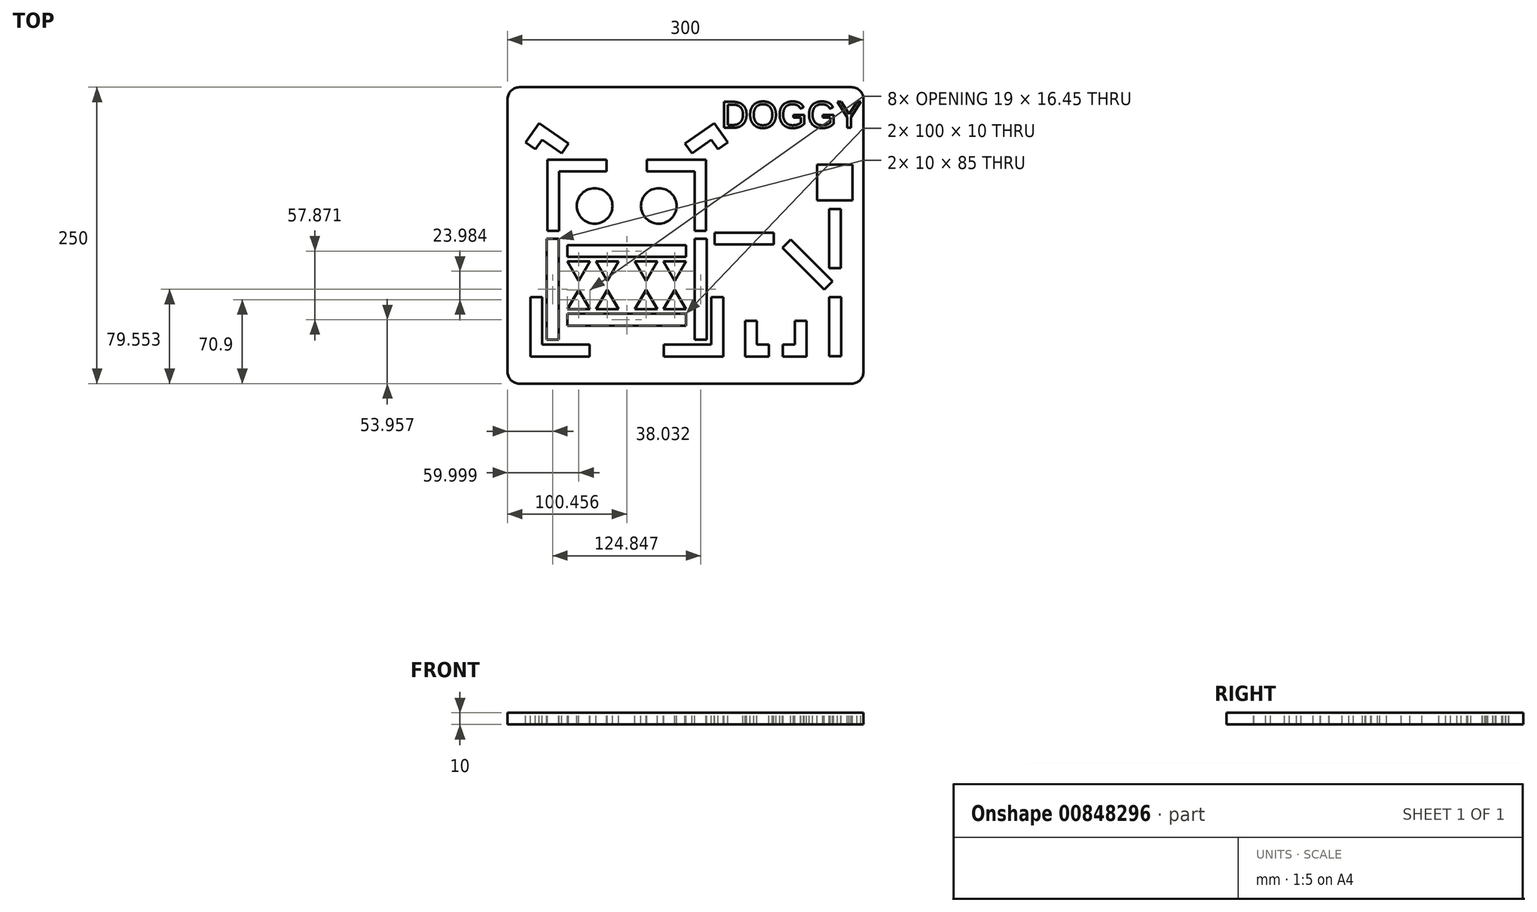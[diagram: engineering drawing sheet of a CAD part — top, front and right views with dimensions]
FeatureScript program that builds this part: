
annotation { "Feature Type Name" : "Feature", "Feature Type Description" : "" }
export const myFeature = defineFeature(function(context is Context, id is Id, definition is map)
    precondition{}
    {
        {
            var Q0;
            Q0=qCreatedBy(makeId("Top.planeOp"),FACE);
            var sketch = newSketch(context, id + "F0", { "sketchPlane" : qUnion([Q0])});
            skLineSegment(sketch, "E0.bottom", {"start": v(-140, 125) * mm, "end": v(140, 125) * mm});
            skLineSegment(sketch, "E0.top", {"start": v(-140, -125) * mm, "end": v(140, -125) * mm});
            skLineSegment(sketch, "E0.left", {"start": v(-150, 115) * mm, "end": v(-150, -115) * mm});
            skLineSegment(sketch, "E0.right", {"start": v(150, 115) * mm, "end": v(150, -115) * mm});
            skPoint(sketch, "E0.middle", {"position": v(0, 0) * mm});
            skPoint(sketch, "E1.visualSharp", {"position": v(-150, 125) * mm});
            skArc(sketch, "E1.filletArc", {"start": v(-140, 125) * mm, "mid": v(-147.07, 122.07) * mm, "end": v(-150, 115) * mm});
            skPoint(sketch, "E2.visualSharp", {"position": v(150, 125) * mm});
            skArc(sketch, "E2.filletArc", {"start": v(150, 115) * mm, "mid": v(147.07, 122.07) * mm, "end": v(140, 125) * mm});
            skPoint(sketch, "E3.visualSharp", {"position": v(150, -125) * mm});
            skArc(sketch, "E3.filletArc", {"start": v(140, -125) * mm, "mid": v(147.07, -122.07) * mm, "end": v(150, -115) * mm});
            skPoint(sketch, "E4.visualSharp", {"position": v(-150, -125) * mm});
            skArc(sketch, "E4.filletArc", {"start": v(-150, -115) * mm, "mid": v(-147.07, -122.07) * mm, "end": v(-140, -125) * mm});
            skSolve(sketch);
        }
        {
            var Q0;
            Q0=makeQuery(id+"F0.imprint","IMPRINT",FACE,{"disambiguationData":[TD([[makeQuery(id+"F0.imprint","IMPRINT",EDGE,{"derivedFrom":sQuery(id+"F0.wireOp",EDGE,"E0.bottom")}),-1.0]])]});
            extrude(context, id + "F1", {"entities" : qUnion([Q0]), "depth" : 10 * mm, "offsetDistance" : 25 * mm});
        }
        {
            var Q0;
            Q0=makeQuery(id+"F1.opExtrude","CAP_FACE",FACE,{"disambiguationData":[OSD([sQuery(id+"F0.wireOp",EDGE,"E0.bottom"),sQuery(id+"F0.wireOp",EDGE,"E0.top"),sQuery(id+"F0.wireOp",EDGE,"E0.left"),sQuery(id+"F0.wireOp",EDGE,"E0.right"),sQuery(id+"F0.wireOp",EDGE,"E1.filletArc"),sQuery(id+"F0.wireOp",EDGE,"E2.filletArc"),sQuery(id+"F0.wireOp",EDGE,"E3.filletArc"),sQuery(id+"F0.wireOp",EDGE,"E4.filletArc")])],"isStart":false});
            var sketch = newSketch(context, id + "F2", { "sketchPlane" : qUnion([Q0])});
            skLineSegment(sketch, "E5.bottom", {"start": v(74.47, -7.65) * mm, "end": v(24.47, -7.65) * mm});
            skLineSegment(sketch, "E5.top", {"start": v(74.47, 2.35) * mm, "end": v(24.47, 2.35) * mm});
            skLineSegment(sketch, "E5.left", {"start": v(74.47, -7.65) * mm, "end": v(74.47, 2.35) * mm});
            skLineSegment(sketch, "E5.right", {"start": v(24.47, -7.65) * mm, "end": v(24.47, 2.35) * mm});
            skPoint(sketch, "E5.middle", {"position": v(49.47, -2.65) * mm});
            skLineSegment(sketch, "E6.bottom", {"start": v(131.14, -51.97) * mm, "end": v(131.14, -101.97) * mm});
            skLineSegment(sketch, "E6.top", {"start": v(121.14, -51.97) * mm, "end": v(121.14, -101.97) * mm});
            skLineSegment(sketch, "E6.left", {"start": v(131.14, -51.97) * mm, "end": v(121.14, -51.97) * mm});
            skLineSegment(sketch, "E6.right", {"start": v(131.14, -101.97) * mm, "end": v(121.14, -101.97) * mm});
            skPoint(sketch, "E6.middle", {"position": v(126.14, -76.97) * mm});
            skLineSegment(sketch, "E7.bottom", {"start": v(88.64, -3.29) * mm, "end": v(124, -38.64) * mm});
            skLineSegment(sketch, "E7.top", {"start": v(81.57, -10.36) * mm, "end": v(116.92, -45.72) * mm});
            skLineSegment(sketch, "E7.left", {"start": v(88.64, -3.29) * mm, "end": v(81.57, -10.36) * mm});
            skLineSegment(sketch, "E7.right", {"start": v(124, -38.64) * mm, "end": v(116.92, -45.72) * mm});
            skPoint(sketch, "E7.middle", {"position": v(102.78, -24.5) * mm});
            skLineSegment(sketch, "E8.bottom", {"start": v(-106.97, -87.95) * mm, "end": v(-116.97, -87.95) * mm});
            skLineSegment(sketch, "E8.top", {"start": v(-106.97, -2.95) * mm, "end": v(-116.97, -2.95) * mm});
            skLineSegment(sketch, "E8.left", {"start": v(-106.97, -87.95) * mm, "end": v(-106.97, -2.95) * mm});
            skLineSegment(sketch, "E8.right", {"start": v(-116.97, -87.95) * mm, "end": v(-116.97, -2.95) * mm});
            skPoint(sketch, "E8.middle", {"position": v(-111.97, -45.45) * mm});
            skLineSegment(sketch, "E9.top", {"start": v(-106.69, 4.02) * mm, "end": v(-116.51, 4.02) * mm});
            skLineSegment(sketch, "E9.left", {"start": v(-106.69, 54.02) * mm, "end": v(-106.69, 4.02) * mm});
            skPoint(sketch, "E9.middle", {"position": v(-111.6, 29.02) * mm});
            skLineSegment(sketch, "E10.top", {"start": v(-116.51, 64.02) * mm, "end": v(-66.51, 64.02) * mm});
            skLineSegment(sketch, "E10.right", {"start": v(-66.51, 54.02) * mm, "end": v(-66.51, 64.02) * mm});
            skLineSegment(sketch, "E11", {"start": v(-106.69, 54.02) * mm, "end": v(-66.51, 54.02) * mm});
            skLineSegment(sketch, "E12", {"start": v(-116.51, 64.02) * mm, "end": v(-116.51, 4.02) * mm});
            skLineSegment(sketch, "E13.bottom", {"start": v(-116.86, 64.03) * mm, "end": v(17.77, 64.03) * mm});
            skLineSegment(sketch, "E14.bottom", {"start": v(-130.81, -52.06) * mm, "end": v(-120.81, -52.06) * mm});
            skLineSegment(sketch, "E14.top", {"start": v(-130.81, -102.06) * mm, "end": v(-120.81, -102.06) * mm});
            skLineSegment(sketch, "E14.left", {"start": v(-130.81, -52.06) * mm, "end": v(-130.81, -102.06) * mm});
            skLineSegment(sketch, "E15.bottom", {"start": v(-130.81, -102.06) * mm, "end": v(-80.81, -102.06) * mm});
            skLineSegment(sketch, "E15.right", {"start": v(-80.81, -102.06) * mm, "end": v(-80.81, -92.06) * mm});
            skLineSegment(sketch, "E16", {"start": v(-120.81, -92.06) * mm, "end": v(-80.81, -92.06) * mm});
            skLineSegment(sketch, "E17", {"start": v(-120.81, -52.06) * mm, "end": v(-120.81, -92.06) * mm});
            skLineSegment(sketch, "E18.MirrorCS", {"start": v(7.6, 54.02) * mm, "end": v(-32.58, 54.02) * mm});
            skLineSegment(sketch, "E19.MirrorCS", {"start": v(-32.58, 54.02) * mm, "end": v(-32.58, 64.02) * mm});
            skLineSegment(sketch, "E20.MirrorCS", {"start": v(17.42, 64.02) * mm, "end": v(-32.58, 64.02) * mm});
            skLineSegment(sketch, "E21.MirrorCS", {"start": v(17.42, 64.02) * mm, "end": v(17.42, 4.02) * mm});
            skLineSegment(sketch, "E22.MirrorCS", {"start": v(7.6, 54.02) * mm, "end": v(7.6, 4.02) * mm});
            skLineSegment(sketch, "E23.MirrorCS", {"start": v(7.6, 4.02) * mm, "end": v(17.42, 4.02) * mm});
            skLineSegment(sketch, "E24.MirrorCS", {"start": v(7.88, -2.95) * mm, "end": v(17.88, -2.95) * mm});
            skLineSegment(sketch, "E25.MirrorCS", {"start": v(7.88, -87.95) * mm, "end": v(7.88, -2.95) * mm});
            skLineSegment(sketch, "E26.MirrorCS", {"start": v(7.88, -87.95) * mm, "end": v(17.88, -87.95) * mm});
            skLineSegment(sketch, "E27.MirrorCS", {"start": v(21.73, -92.06) * mm, "end": v(-18.27, -92.06) * mm});
            skLineSegment(sketch, "E28.MirrorCS", {"start": v(-18.27, -102.06) * mm, "end": v(-18.27, -92.06) * mm});
            skLineSegment(sketch, "E29.MirrorCS", {"start": v(31.73, -102.06) * mm, "end": v(-18.27, -102.06) * mm});
            skLineSegment(sketch, "E30.MirrorCS", {"start": v(31.73, -52.06) * mm, "end": v(31.73, -102.06) * mm});
            skLineSegment(sketch, "E31.MirrorCS", {"start": v(31.73, -52.06) * mm, "end": v(21.73, -52.06) * mm});
            skLineSegment(sketch, "E32.MirrorCS", {"start": v(21.73, -52.06) * mm, "end": v(21.73, -92.06) * mm});
            skLineSegment(sketch, "E33.left", {"start": v(-99.54, -8.17) * mm, "end": v(-99.54, -18.17) * mm});
            skLineSegment(sketch, "E33.right", {"start": v(-49.54, 23.63) * mm, "end": v(-49.54, 13.63) * mm});
            skLineSegment(sketch, "E34.MirrorCS", {"start": v(0.46, -8.17) * mm, "end": v(0.46, -18.17) * mm});
            skLineSegment(sketch, "E35", {"start": v(-99.54, -8.17) * mm, "end": v(0.46, -8.17) * mm});
            skLineSegment(sketch, "E36", {"start": v(-99.54, -18.17) * mm, "end": v(0.46, -18.17) * mm});
            skCircle(sketch, "E37", {"center": v(-76.58, 24.84) * mm, "radius": 15 * mm});
            skCircle(sketch, "E38.MirrorC", {"center": v(-22.5, 24.84) * mm, "radius": 15 * mm});
            skLineSegment(sketch, "E39", {"start": v(17.88, -2.95) * mm, "end": v(17.88, -87.95) * mm});
            skLineSegment(sketch, "E40.right", {"start": v(70.28, -92.05) * mm, "end": v(70.28, -102.05) * mm});
            skPoint(sketch, "E41.oppositeSnap0", {"position": v(60.28, -92.05) * mm});
            skLineSegment(sketch, "E41.top", {"start": v(50.28, -72.05) * mm, "end": v(60.28, -72.05) * mm});
            skLineSegment(sketch, "E41.left", {"start": v(50.28, -102.05) * mm, "end": v(50.28, -72.05) * mm});
            skLineSegment(sketch, "E42.right", {"start": v(82.04, -102.05) * mm, "end": v(82.04, -92.05) * mm});
            skLineSegment(sketch, "E43.top", {"start": v(102.04, -72.05) * mm, "end": v(92.04, -72.05) * mm});
            skLineSegment(sketch, "E43.left", {"start": v(102.04, -102.05) * mm, "end": v(102.04, -72.05) * mm});
            skLineSegment(sketch, "E44", {"start": v(60.28, -92.05) * mm, "end": v(70.28, -92.05) * mm});
            skLineSegment(sketch, "E45", {"start": v(60.28, -72.05) * mm, "end": v(60.28, -92.05) * mm});
            skLineSegment(sketch, "E46", {"start": v(50.28, -102.05) * mm, "end": v(70.28, -102.05) * mm});
            skLineSegment(sketch, "E47", {"start": v(92.04, -72.05) * mm, "end": v(92.04, -92.05) * mm});
            skLineSegment(sketch, "E48", {"start": v(82.04, -102.05) * mm, "end": v(102.04, -102.05) * mm});
            skLineSegment(sketch, "E49", {"start": v(92.04, -92.05) * mm, "end": v(82.04, -92.05) * mm});
            skLineSegment(sketch, "E50.right", {"start": v(-126.57, 72.66) * mm, "end": v(-134.76, 78.4) * mm});
            skPoint(sketch, "E51.oppositeSnap0", {"position": v(-120.83, 80.85) * mm});
            skLineSegment(sketch, "E51.top", {"start": v(-98.71, 77.57) * mm, "end": v(-104.45, 69.38) * mm});
            skLineSegment(sketch, "E51.left", {"start": v(-123.29, 94.78) * mm, "end": v(-98.71, 77.57) * mm});
            skLineSegment(sketch, "E52", {"start": v(-120.83, 80.85) * mm, "end": v(-126.57, 72.66) * mm});
            skLineSegment(sketch, "E53", {"start": v(-104.45, 69.38) * mm, "end": v(-120.83, 80.85) * mm});
            skLineSegment(sketch, "E54", {"start": v(-123.29, 94.78) * mm, "end": v(-134.76, 78.4) * mm});
            skLineSegment(sketch, "E55.0", {"start": v(-90, -38.34) * mm, "end": v(-99.5, -21.89) * mm});
            skLineSegment(sketch, "E55.1", {"start": v(-99.5, -21.89) * mm, "end": v(-80.5, -21.89) * mm});
            skLineSegment(sketch, "E55.2", {"start": v(-80.5, -21.89) * mm, "end": v(-90, -38.34) * mm});
            skLineSegment(sketch, "E56.0", {"start": v(-65.83, -38.34) * mm, "end": v(-75.33, -21.89) * mm});
            skLineSegment(sketch, "E56.1", {"start": v(-75.33, -21.89) * mm, "end": v(-56.33, -21.89) * mm});
            skLineSegment(sketch, "E56.2", {"start": v(-56.33, -21.89) * mm, "end": v(-65.83, -38.34) * mm});
            skLineSegment(sketch, "E57.MirrorCS", {"start": v(-23.75, -21.89) * mm, "end": v(-42.75, -21.89) * mm});
            skLineSegment(sketch, "E58.MirrorCS", {"start": v(-33.25, -38.34) * mm, "end": v(-23.75, -21.89) * mm});
            skLineSegment(sketch, "E59.MirrorCS", {"start": v(-42.75, -21.89) * mm, "end": v(-33.25, -38.34) * mm});
            skLineSegment(sketch, "E60.MirrorCS", {"start": v(-9.09, -38.34) * mm, "end": v(0.41, -21.89) * mm});
            skLineSegment(sketch, "E61.MirrorCS", {"start": v(-18.59, -21.89) * mm, "end": v(-9.09, -38.34) * mm});
            skLineSegment(sketch, "E62.MirrorCS", {"start": v(0.41, -21.89) * mm, "end": v(-18.59, -21.89) * mm});
            skLineSegment(sketch, "E63.MirrorCS", {"start": v(-90, -45.87) * mm, "end": v(-99.5, -62.33) * mm});
            skLineSegment(sketch, "E64.MirrorCS", {"start": v(-99.5, -62.33) * mm, "end": v(-80.5, -62.33) * mm});
            skLineSegment(sketch, "E65.MirrorCS", {"start": v(-80.5, -62.33) * mm, "end": v(-90, -45.87) * mm});
            skLineSegment(sketch, "E66.MirrorCS", {"start": v(-65.83, -45.87) * mm, "end": v(-75.33, -62.33) * mm});
            skLineSegment(sketch, "E67.MirrorCS", {"start": v(-56.33, -62.33) * mm, "end": v(-65.83, -45.87) * mm});
            skLineSegment(sketch, "E68.MirrorCS", {"start": v(-75.33, -62.33) * mm, "end": v(-56.33, -62.33) * mm});
            skLineSegment(sketch, "E69.MirrorCS", {"start": v(-23.75, -62.33) * mm, "end": v(-42.75, -62.33) * mm});
            skLineSegment(sketch, "E70.MirrorCS", {"start": v(-42.75, -62.33) * mm, "end": v(-33.25, -45.87) * mm});
            skLineSegment(sketch, "E71.MirrorCS", {"start": v(-33.25, -45.87) * mm, "end": v(-23.75, -62.33) * mm});
            skLineSegment(sketch, "E72.MirrorCS", {"start": v(-9.09, -45.87) * mm, "end": v(0.41, -62.33) * mm});
            skLineSegment(sketch, "E73.MirrorCS", {"start": v(-18.59, -62.33) * mm, "end": v(-9.09, -45.87) * mm});
            skLineSegment(sketch, "E74.MirrorCS", {"start": v(0.41, -62.33) * mm, "end": v(-18.59, -62.33) * mm});
            skLineSegment(sketch, "E75.MirrorCS", {"start": v(-99.54, -76.04) * mm, "end": v(0.46, -76.04) * mm});
            skLineSegment(sketch, "E76.MirrorCS", {"start": v(-99.54, -66.04) * mm, "end": v(0.46, -66.04) * mm});
            skLineSegment(sketch, "E77.MirrorCS", {"start": v(-99.54, -76.04) * mm, "end": v(-99.54, -66.04) * mm});
            skLineSegment(sketch, "E78.MirrorCS", {"start": v(0.46, -76.04) * mm, "end": v(0.46, -66.04) * mm});
            skLineSegment(sketch, "E79", {"start": v(-49.54, 64.03) * mm, "end": v(-49.54, 121.25) * mm});
            skLineSegment(sketch, "E80", {"start": v(-49.54, 121.25) * mm, "end": v(-49.54, -111.51) * mm});
            skLineSegment(sketch, "E81.MirrorCS", {"start": v(24.2, 94.78) * mm, "end": v(-0.37, 77.57) * mm});
            skLineSegment(sketch, "E82.MirrorCS", {"start": v(-0.37, 77.57) * mm, "end": v(5.36, 69.38) * mm});
            skLineSegment(sketch, "E83.MirrorCS", {"start": v(27.48, 72.66) * mm, "end": v(35.67, 78.4) * mm});
            skLineSegment(sketch, "E84.MirrorCS", {"start": v(24.2, 94.78) * mm, "end": v(35.67, 78.4) * mm});
            skLineSegment(sketch, "E85.MirrorCS", {"start": v(21.74, 80.85) * mm, "end": v(27.48, 72.66) * mm});
            skLineSegment(sketch, "E86", {"start": v(5.36, 69.38) * mm, "end": v(21.74, 80.85) * mm});
            skLineSegment(sketch, "E87.bottom", {"start": v(131, 22.35) * mm, "end": v(131, -27.65) * mm});
            skLineSegment(sketch, "E87.top", {"start": v(121, 22.35) * mm, "end": v(121, -27.65) * mm});
            skLineSegment(sketch, "E87.left", {"start": v(131, 22.35) * mm, "end": v(121, 22.35) * mm});
            skLineSegment(sketch, "E87.right", {"start": v(131, -27.65) * mm, "end": v(121, -27.65) * mm});
            skPoint(sketch, "E87.middle", {"position": v(126, -2.65) * mm});
            skLineSegment(sketch, "E88.bottom", {"start": v(110.85, 59.68) * mm, "end": v(140.85, 59.68) * mm});
            skLineSegment(sketch, "E88.top", {"start": v(110.85, 29.68) * mm, "end": v(140.85, 29.68) * mm});
            skLineSegment(sketch, "E88.left", {"start": v(110.85, 59.68) * mm, "end": v(110.85, 29.68) * mm});
            skLineSegment(sketch, "E88.right", {"start": v(140.85, 59.68) * mm, "end": v(140.85, 29.68) * mm});
            skText(sketch, "E89", { "text": "DOGGY", "fontName": "Arimo-Regular.ttf"});
            const initialGuessF2  = {"E89": [0.03, 0.09081, 1, 0, 0.02292]};
            skSetInitialGuess(sketch, initialGuessF2);
            skSolve(sketch);
        }
        {
            var Q0;
            Q0 = qSketchRegion(id + "F2", true);
            extrude(context, id + "F3", {"entities" : qUnion([Q0]), "operationType" : NewBodyOperationType.REMOVE, "oppositeDirection" : true, "depth" : 10 * mm, "offsetDistance" : 25 * mm});
        }
    });
